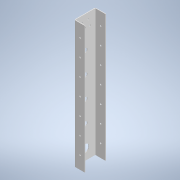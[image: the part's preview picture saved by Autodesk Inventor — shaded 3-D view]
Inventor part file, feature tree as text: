
AUTODESK INVENTOR PART (.ipt)
format: ipt  version: 2022 (Build 260153000, 153)  size: 259,584 bytes
history: native  units: mm
features: sketch x5, projected_geometry x4, sheet_metal_op x3, extrude x3, other x3
ambient origin geometry x8: Origin, YZ Plane, XZ Plane, XY Plane, X Axis, Y Axis, Z Axis, Center Point
bodies: Solid1 (feature_tree)
feature tree (18):
  sheet_metal_op  "Contour Flange1"
  extrude  "Extrusion3"  Depth=25.0mm
  extrude  "Extrusion4"  Depth=1.5mm
  extrude  "Extrusion5"  Depth=1.5mm
  sketch  "Sketch1"  dims[d0=50.0mm d1=25.0mm]
  other  "Plate1"
  sheet_metal_op  "Bend1"
  sheet_metal_op  "Corner1"
  sketch  "Sketch2"  dims[d2=25.0mm d3=1.5mm]
  projected_geometry  "Projected Loop1"
  sketch  "Sketch8"  dims[d4=1.5mm d5=0.75mm]
  projected_geometry  "Projected Loop9"
  sketch  "Sketch9"  dims[d6=3.0mm]
  projected_geometry  "Projected Loop10"
  sketch  "Sketch10"  dims[d7=1.5mm d8=300.0mm d9=1.5mm d10=0.5mm d11=6.0mm d12=1.5mm d13=1.5mm d14=10.0mm d15=25.0mm d16=22.0mm d17=50.0mm d19=50.0mm d20=10.0mm d22=10.0mm d24=1.5mm d25=0.0mm d33=44.0mm d34=3.35mm d35=3.35mm d36=3.35mm d37=3.35mm d38=3.35mm d39=44.0mm d40=14.666667mm d43=14.666667mm d46=14.666667mm d47=11.0mm d48=11.0mm d49=11.0mm d50=10.0mm d51=0.0mm d52=14.666667mm d53=14.666667mm d54=14.666667mm d55=14.666667mm d56=14.666667mm d57=14.666667mm d58=3.35mm d59=30.0mm d60=70.0mm d62=40.0mm d63=10.0mm d65=10.0mm d67=0.0mm d68=0.0mm d69=18.1mm d70=0.0mm d71=0.0mm]
  projected_geometry  "Projected Loop11"
  other  "Cut1"
  other  "Definition1"
